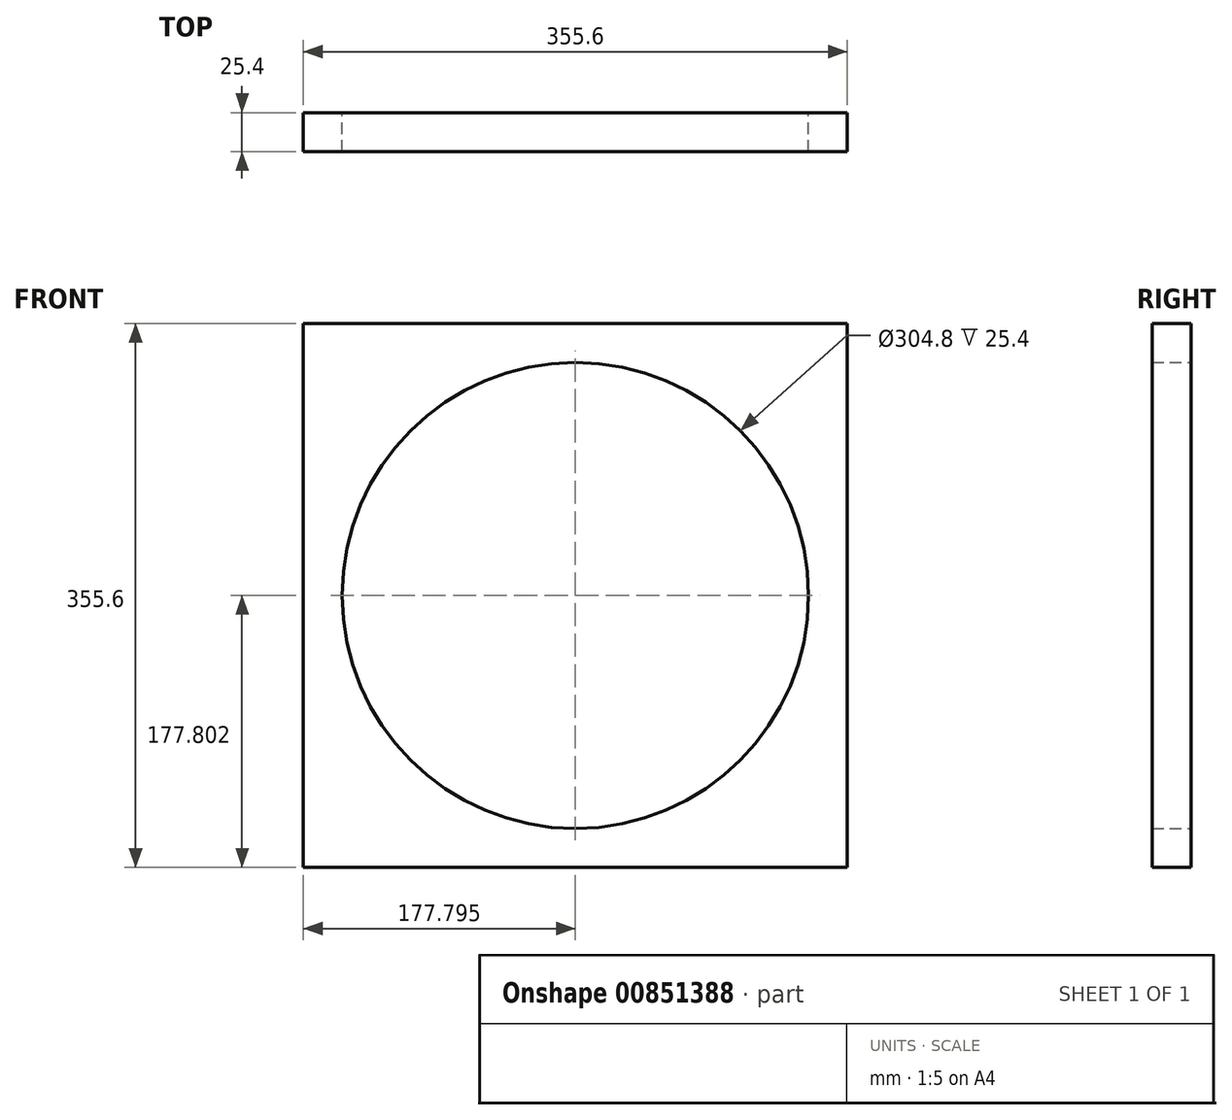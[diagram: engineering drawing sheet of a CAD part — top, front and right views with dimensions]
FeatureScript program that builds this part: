
annotation { "Feature Type Name" : "Feature", "Feature Type Description" : "" }
export const myFeature = defineFeature(function(context is Context, id is Id, definition is map)
    precondition{}
    {
        {
            var Q0;
            Q0=qCreatedBy(makeId("Front.planeOp"),FACE);
            var sketch = newSketch(context, id + "F0", { "sketchPlane" : qUnion([Q0])});
            skLineSegment(sketch, "E0.bottom", {"start": v(-187.37, 203.51) * mm, "end": v(168.23, 203.51) * mm});
            skLineSegment(sketch, "E0.top", {"start": v(-187.37, -152.09) * mm, "end": v(168.23, -152.09) * mm});
            skLineSegment(sketch, "E0.left", {"start": v(-187.37, 203.51) * mm, "end": v(-187.37, -152.09) * mm});
            skLineSegment(sketch, "E0.right", {"start": v(168.23, 203.51) * mm, "end": v(168.23, -152.09) * mm});
            skCircle(sketch, "E1", {"center": v(-9.57, 25.71) * mm, "radius": 152.4 * mm});
            skSolve(sketch);
        }
        {
            var Q0;
            Q0 = qSketchRegion(id + "F0", true);
            extrude(context, id + "F1", {"entities" : qUnion([Q0]), "depth" : 25.4 * mm, "offsetDistance" : 25.4 * mm});
        }
    });
